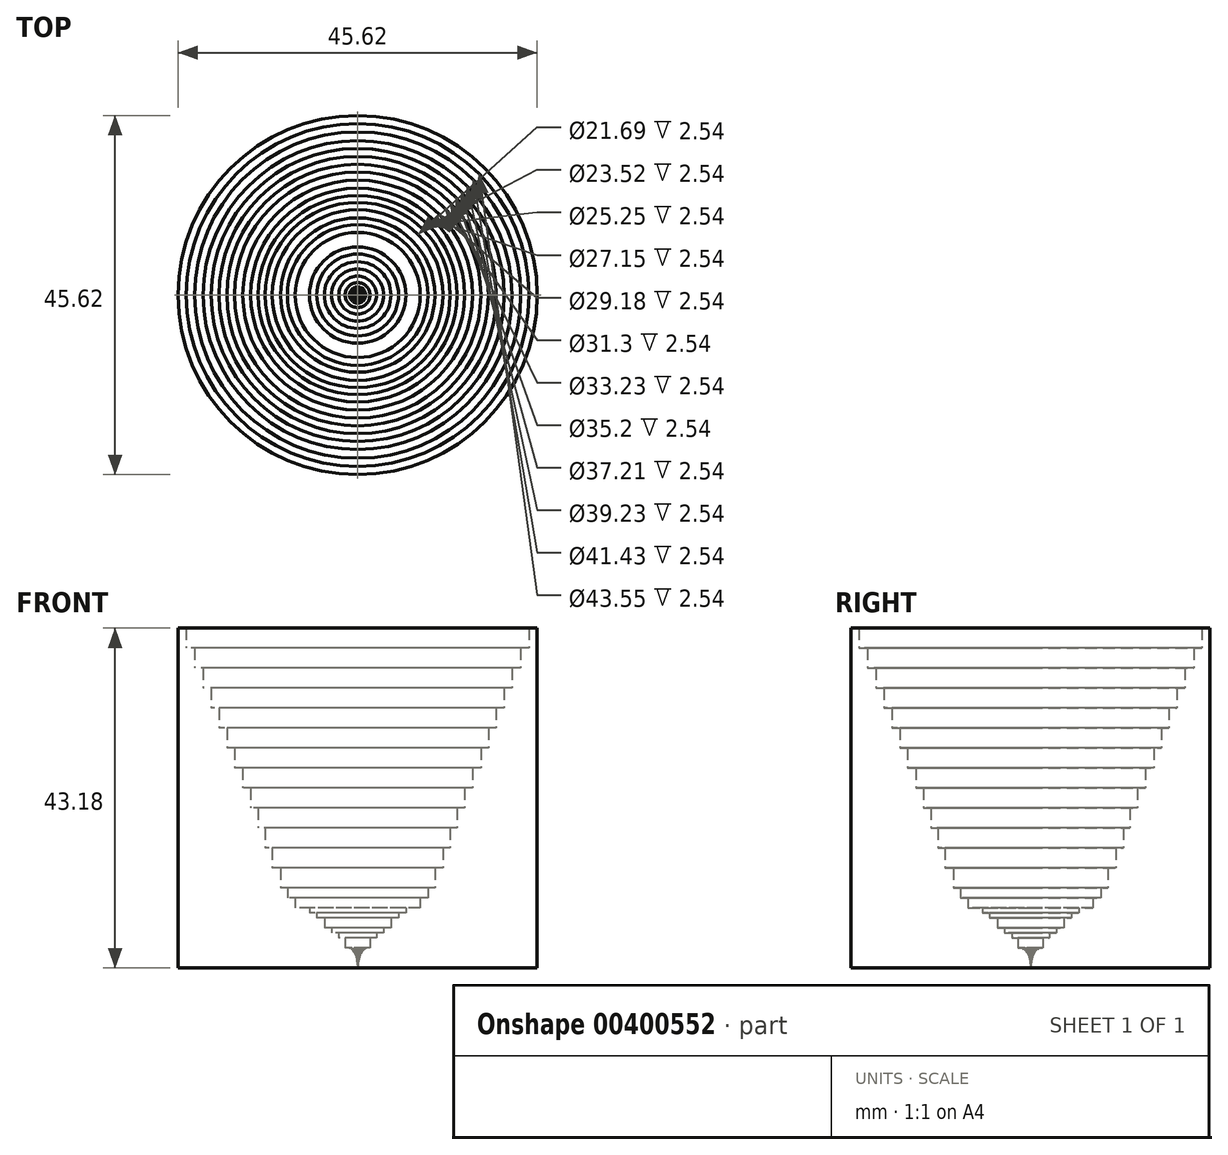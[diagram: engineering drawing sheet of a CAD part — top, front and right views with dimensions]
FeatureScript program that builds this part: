
annotation { "Feature Type Name" : "Feature", "Feature Type Description" : "" }
export const myFeature = defineFeature(function(context is Context, id is Id, definition is map)
    precondition{}
    {
        {
            var Q0;
            Q0=qCreatedBy(makeId("Top.planeOp"),FACE);
            var sketch = newSketch(context, id + "F0", { "sketchPlane" : qUnion([Q0])});
            skCircle(sketch, "E0", {"center": v(0, 0) * mm, "radius": 22.8 * mm});
            skCircle(sketch, "E1", {"center": v(0, 0) * mm, "radius": 21.78 * mm});
            skCircle(sketch, "E2", {"center": v(0, 0) * mm, "radius": 20.72 * mm});
            skCircle(sketch, "E3", {"center": v(0, 0) * mm, "radius": 19.62 * mm});
            skCircle(sketch, "E4", {"center": v(0, 0) * mm, "radius": 18.6 * mm});
            skCircle(sketch, "E5", {"center": v(0, 0) * mm, "radius": 17.6 * mm});
            skCircle(sketch, "E6", {"center": v(0, 0) * mm, "radius": 16.61 * mm});
            skCircle(sketch, "E7", {"center": v(0, 0) * mm, "radius": 15.65 * mm});
            skCircle(sketch, "E8", {"center": v(0, 0) * mm, "radius": 14.59 * mm});
            skCircle(sketch, "E9", {"center": v(0, 0) * mm, "radius": 13.57 * mm});
            skCircle(sketch, "E10", {"center": v(0, 0) * mm, "radius": 12.63 * mm});
            skCircle(sketch, "E11", {"center": v(0, 0) * mm, "radius": 11.76 * mm});
            skCircle(sketch, "E12", {"center": v(0, 0) * mm, "radius": 10.84 * mm});
            skCircle(sketch, "E13", {"center": v(0, 0) * mm, "radius": 9.8 * mm});
            skCircle(sketch, "E14", {"center": v(0, 0) * mm, "radius": 8.92 * mm});
            skCircle(sketch, "E15", {"center": v(0, 0) * mm, "radius": 7.94 * mm});
            skCircle(sketch, "E16", {"center": v(0, 0) * mm, "radius": 7.05 * mm});
            skCircle(sketch, "E17", {"center": v(0, 0) * mm, "radius": 6.12 * mm});
            skCircle(sketch, "E18", {"center": v(0, 0) * mm, "radius": 5.2 * mm});
            skCircle(sketch, "E19", {"center": v(0, 0) * mm, "radius": 4.23 * mm});
            skCircle(sketch, "E20", {"center": v(0, 0) * mm, "radius": 3.3 * mm});
            skCircle(sketch, "E21", {"center": v(0, 0) * mm, "radius": 2.4 * mm});
            skCircle(sketch, "E22", {"center": v(0, 0) * mm, "radius": 1.58 * mm});
            skCircle(sketch, "E23", {"center": v(0, 0) * mm, "radius": 1.03 * mm});
            skCircle(sketch, "E24", {"center": v(0, 0) * mm, "radius": 0.8 * mm});
            skCircle(sketch, "E25", {"center": v(0, 0) * mm, "radius": 0.67 * mm});
            skCircle(sketch, "E26", {"center": v(0, 0) * mm, "radius": 0.58 * mm});
            skCircle(sketch, "E27", {"center": v(0, 0) * mm, "radius": 0.49 * mm});
            skCircle(sketch, "E28", {"center": v(0, 0) * mm, "radius": 0.4 * mm});
            skCircle(sketch, "E29", {"center": v(0, 0) * mm, "radius": 0.34 * mm});
            skCircle(sketch, "E30", {"center": v(0, 0) * mm, "radius": 0.27 * mm});
            skCircle(sketch, "E31", {"center": v(0, 0) * mm, "radius": 0.22 * mm});
            skCircle(sketch, "E32", {"center": v(0, 0) * mm, "radius": 0.17 * mm});
            skCircle(sketch, "E33", {"center": v(0, 0) * mm, "radius": 0.11 * mm});
            skCircle(sketch, "E34", {"center": v(0, 0) * mm, "radius": 0.08 * mm});
            skCircle(sketch, "E35", {"center": v(0, 0) * mm, "radius": 0.06 * mm});
            skCircle(sketch, "E36", {"center": v(0, 0) * mm, "radius": 0.04 * mm});
            skCircle(sketch, "E37", {"center": v(0, 0) * mm, "radius": 0.03 * mm});
            skCircle(sketch, "E38", {"center": v(0, 0) * mm, "radius": 0.02 * mm});
            skSolve(sketch);
        }
        {
            var Q0;
            Q0=makeQuery(id+"F0.imprint","IMPRINT",FACE,{"disambiguationData":[TD([[makeQuery(id+"F0.imprint","IMPRINT",EDGE,{"derivedFrom":sQuery(id+"F0.wireOp",EDGE,"E38")}),1.0]])]});
            extrude(context, id + "F1", {"entities" : qUnion([Q0]), "depth" : 0.13 * mm});
        }
        {
            var Q0;
            Q0=makeQuery(id+"F0.imprint","IMPRINT",FACE,{"disambiguationData":[TD([[makeQuery(id+"F0.imprint","IMPRINT",EDGE,{"derivedFrom":sQuery(id+"F0.wireOp",EDGE,"E37")}),1.0]])]});
            extrude(context, id + "F2", {"entities" : qUnion([Q0]), "operationType" : NewBodyOperationType.ADD, "depth" : 0.25 * mm});
        }
        {
            var Q0;
            Q0=makeQuery(id+"F0.imprint","IMPRINT",FACE,{"disambiguationData":[TD([[makeQuery(id+"F0.imprint","IMPRINT",EDGE,{"derivedFrom":sQuery(id+"F0.wireOp",EDGE,"E36")}),1.0]])]});
            extrude(context, id + "F3", {"entities" : qUnion([Q0]), "operationType" : NewBodyOperationType.ADD, "depth" : 0.38 * mm});
        }
        {
            var Q0;
            Q0=makeQuery(id+"F0.imprint","IMPRINT",FACE,{"disambiguationData":[TD([[makeQuery(id+"F0.imprint","IMPRINT",EDGE,{"derivedFrom":sQuery(id+"F0.wireOp",EDGE,"E35")}),1.0]])]});
            extrude(context, id + "F4", {"entities" : qUnion([Q0]), "operationType" : NewBodyOperationType.ADD, "depth" : 0.5 * mm});
        }
        {
            var Q0;
            Q0=makeQuery(id+"F0.imprint","IMPRINT",FACE,{"disambiguationData":[TD([[makeQuery(id+"F0.imprint","IMPRINT",EDGE,{"derivedFrom":sQuery(id+"F0.wireOp",EDGE,"E34")}),1.0]])]});
            extrude(context, id + "F5", {"entities" : qUnion([Q0]), "operationType" : NewBodyOperationType.ADD, "depth" : 0.64 * mm});
        }
        {
            var Q0;
            Q0=makeQuery(id+"F0.imprint","IMPRINT",FACE,{"disambiguationData":[TD([[makeQuery(id+"F0.imprint","IMPRINT",EDGE,{"derivedFrom":sQuery(id+"F0.wireOp",EDGE,"E33")}),1.0]])]});
            extrude(context, id + "F6", {"entities" : qUnion([Q0]), "operationType" : NewBodyOperationType.ADD, "depth" : 0.76 * mm});
        }
        {
            var Q0;
            Q0=makeQuery(id+"F0.imprint","IMPRINT",FACE,{"disambiguationData":[TD([[makeQuery(id+"F0.imprint","IMPRINT",EDGE,{"derivedFrom":sQuery(id+"F0.wireOp",EDGE,"E32")}),1.0]])]});
            extrude(context, id + "F7", {"entities" : qUnion([Q0]), "operationType" : NewBodyOperationType.ADD, "depth" : 1.02 * mm});
        }
        {
            var Q0;
            Q0=makeQuery(id+"F0.imprint","IMPRINT",FACE,{"disambiguationData":[TD([[makeQuery(id+"F0.imprint","IMPRINT",EDGE,{"derivedFrom":sQuery(id+"F0.wireOp",EDGE,"E31")}),1.0]])]});
            extrude(context, id + "F8", {"entities" : qUnion([Q0]), "operationType" : NewBodyOperationType.ADD, "depth" : 1.27 * mm});
        }
        {
            var Q0;
            Q0=makeQuery(id+"F0.imprint","IMPRINT",FACE,{"disambiguationData":[TD([[makeQuery(id+"F0.imprint","IMPRINT",EDGE,{"derivedFrom":sQuery(id+"F0.wireOp",EDGE,"E30")}),1.0]])]});
            extrude(context, id + "F9", {"entities" : qUnion([Q0]), "operationType" : NewBodyOperationType.ADD, "depth" : 1.52 * mm});
        }
        {
            var Q0;
            Q0=makeQuery(id+"F0.imprint","IMPRINT",FACE,{"disambiguationData":[TD([[makeQuery(id+"F0.imprint","IMPRINT",EDGE,{"derivedFrom":sQuery(id+"F0.wireOp",EDGE,"E29")}),1.0]])]});
            extrude(context, id + "F10", {"entities" : qUnion([Q0]), "operationType" : NewBodyOperationType.ADD, "depth" : 1.65 * mm});
        }
        {
            var Q0;
            Q0=makeQuery(id+"F0.imprint","IMPRINT",FACE,{"disambiguationData":[TD([[makeQuery(id+"F0.imprint","IMPRINT",EDGE,{"derivedFrom":sQuery(id+"F0.wireOp",EDGE,"E28")}),1.0]])]});
            extrude(context, id + "F11", {"entities" : qUnion([Q0]), "operationType" : NewBodyOperationType.ADD, "depth" : 1.78 * mm});
        }
        {
            var Q0;
            Q0=makeQuery(id+"F0.imprint","IMPRINT",FACE,{"disambiguationData":[TD([[makeQuery(id+"F0.imprint","IMPRINT",EDGE,{"derivedFrom":sQuery(id+"F0.wireOp",EDGE,"E27")}),1.0]])]});
            extrude(context, id + "F12", {"entities" : qUnion([Q0]), "operationType" : NewBodyOperationType.ADD, "depth" : 1.9 * mm});
        }
        {
            var Q0;
            Q0=makeQuery(id+"F0.imprint","IMPRINT",FACE,{"disambiguationData":[TD([[makeQuery(id+"F0.imprint","IMPRINT",EDGE,{"derivedFrom":sQuery(id+"F0.wireOp",EDGE,"E26")}),1.0]])]});
            extrude(context, id + "F13", {"entities" : qUnion([Q0]), "operationType" : NewBodyOperationType.ADD, "depth" : 2.03 * mm});
        }
        {
            var Q0;
            Q0=makeQuery(id+"F0.imprint","IMPRINT",FACE,{"disambiguationData":[TD([[makeQuery(id+"F0.imprint","IMPRINT",EDGE,{"derivedFrom":sQuery(id+"F0.wireOp",EDGE,"E25")}),1.0]])]});
            extrude(context, id + "F14", {"entities" : qUnion([Q0]), "operationType" : NewBodyOperationType.ADD, "depth" : 2.16 * mm});
        }
        {
            var Q0;
            Q0=makeQuery(id+"F0.imprint","IMPRINT",FACE,{"disambiguationData":[TD([[makeQuery(id+"F0.imprint","IMPRINT",EDGE,{"derivedFrom":sQuery(id+"F0.wireOp",EDGE,"E24")}),1.0]])]});
            extrude(context, id + "F15", {"entities" : qUnion([Q0]), "operationType" : NewBodyOperationType.ADD, "depth" : 2.3 * mm});
        }
        {
            var Q0;
            Q0=makeQuery(id+"F0.imprint","IMPRINT",FACE,{"disambiguationData":[TD([[makeQuery(id+"F0.imprint","IMPRINT",EDGE,{"derivedFrom":sQuery(id+"F0.wireOp",EDGE,"E23")}),1.0]])]});
            extrude(context, id + "F16", {"entities" : qUnion([Q0]), "operationType" : NewBodyOperationType.ADD, "depth" : 2.41 * mm});
        }
        {
            var Q0;
            Q0=makeQuery(id+"F0.imprint","IMPRINT",FACE,{"disambiguationData":[TD([[makeQuery(id+"F0.imprint","IMPRINT",EDGE,{"derivedFrom":sQuery(id+"F0.wireOp",EDGE,"E22")}),1.0]])]});
            extrude(context, id + "F17", {"entities" : qUnion([Q0]), "operationType" : NewBodyOperationType.ADD, "depth" : 2.54 * mm});
        }
        {
            var Q0;
            Q0=makeQuery(id+"F0.imprint","IMPRINT",FACE,{"disambiguationData":[TD([[makeQuery(id+"F0.imprint","IMPRINT",EDGE,{"derivedFrom":sQuery(id+"F0.wireOp",EDGE,"E21")}),1.0]])]});
            extrude(context, id + "F18", {"entities" : qUnion([Q0]), "operationType" : NewBodyOperationType.ADD, "depth" : 3.8 * mm});
        }
        {
            var Q0;
            Q0=makeQuery(id+"F0.imprint","IMPRINT",FACE,{"disambiguationData":[TD([[makeQuery(id+"F0.imprint","IMPRINT",EDGE,{"derivedFrom":sQuery(id+"F0.wireOp",EDGE,"E20")}),1.0]])]});
            extrude(context, id + "F19", {"entities" : qUnion([Q0]), "operationType" : NewBodyOperationType.ADD, "depth" : 4.44 * mm});
        }
        {
            var Q0;
            Q0=makeQuery(id+"F0.imprint","IMPRINT",FACE,{"disambiguationData":[TD([[makeQuery(id+"F0.imprint","IMPRINT",EDGE,{"derivedFrom":sQuery(id+"F0.wireOp",EDGE,"E19")}),1.0]])]});
            extrude(context, id + "F20", {"entities" : qUnion([Q0]), "operationType" : NewBodyOperationType.ADD, "depth" : 5.08 * mm});
        }
        {
            var Q0;
            Q0=makeQuery(id+"F0.imprint","IMPRINT",FACE,{"disambiguationData":[TD([[makeQuery(id+"F0.imprint","IMPRINT",EDGE,{"derivedFrom":sQuery(id+"F0.wireOp",EDGE,"E18")}),1.0]])]});
            extrude(context, id + "F21", {"entities" : qUnion([Q0]), "operationType" : NewBodyOperationType.ADD, "depth" : 6.35 * mm});
        }
        {
            var Q0;
            Q0=makeQuery(id+"F0.imprint","IMPRINT",FACE,{"disambiguationData":[TD([[makeQuery(id+"F0.imprint","IMPRINT",EDGE,{"derivedFrom":sQuery(id+"F0.wireOp",EDGE,"E17")}),1.0]])]});
            extrude(context, id + "F22", {"entities" : qUnion([Q0]), "operationType" : NewBodyOperationType.ADD, "depth" : 7 * mm});
        }
        {
            var Q0;
            Q0=makeQuery(id+"F0.imprint","IMPRINT",FACE,{"disambiguationData":[TD([[makeQuery(id+"F0.imprint","IMPRINT",EDGE,{"derivedFrom":sQuery(id+"F0.wireOp",EDGE,"E16")}),1.0]])]});
            extrude(context, id + "F23", {"entities" : qUnion([Q0]), "operationType" : NewBodyOperationType.ADD, "depth" : 7.62 * mm});
        }
        {
            var Q0;
            Q0=makeQuery(id+"F0.imprint","IMPRINT",FACE,{"disambiguationData":[TD([[makeQuery(id+"F0.imprint","IMPRINT",EDGE,{"derivedFrom":sQuery(id+"F0.wireOp",EDGE,"E15")}),1.0]])]});
            extrude(context, id + "F24", {"entities" : qUnion([Q0]), "operationType" : NewBodyOperationType.ADD, "depth" : 7.62 * mm});
        }
        {
            var Q0;
            Q0=makeQuery(id+"F0.imprint","IMPRINT",FACE,{"disambiguationData":[TD([[makeQuery(id+"F0.imprint","IMPRINT",EDGE,{"derivedFrom":sQuery(id+"F0.wireOp",EDGE,"E14")}),1.0]])]});
            extrude(context, id + "F25", {"entities" : qUnion([Q0]), "operationType" : NewBodyOperationType.ADD, "depth" : 8.9 * mm});
        }
        {
            var Q0;
            Q0=makeQuery(id+"F0.imprint","IMPRINT",FACE,{"disambiguationData":[TD([[makeQuery(id+"F0.imprint","IMPRINT",EDGE,{"derivedFrom":sQuery(id+"F0.wireOp",EDGE,"E13")}),1.0]])]});
            extrude(context, id + "F26", {"entities" : qUnion([Q0]), "operationType" : NewBodyOperationType.ADD, "depth" : 10.16 * mm});
        }
        {
            var Q0;
            Q0=makeQuery(id+"F0.imprint","IMPRINT",FACE,{"disambiguationData":[TD([[makeQuery(id+"F0.imprint","IMPRINT",EDGE,{"derivedFrom":sQuery(id+"F0.wireOp",EDGE,"E12")}),1.0]])]});
            extrude(context, id + "F27", {"entities" : qUnion([Q0]), "operationType" : NewBodyOperationType.ADD, "depth" : 12.7 * mm});
        }
        {
            var Q0;
            Q0=makeQuery(id+"F0.imprint","IMPRINT",FACE,{"disambiguationData":[TD([[makeQuery(id+"F0.imprint","IMPRINT",EDGE,{"derivedFrom":sQuery(id+"F0.wireOp",EDGE,"E11")}),1.0]])]});
            extrude(context, id + "F28", {"entities" : qUnion([Q0]), "operationType" : NewBodyOperationType.ADD, "depth" : 15.24 * mm});
        }
        {
            var Q0;
            Q0=makeQuery(id+"F0.imprint","IMPRINT",FACE,{"disambiguationData":[TD([[makeQuery(id+"F0.imprint","IMPRINT",EDGE,{"derivedFrom":sQuery(id+"F0.wireOp",EDGE,"E10")}),1.0]])]});
            extrude(context, id + "F29", {"entities" : qUnion([Q0]), "operationType" : NewBodyOperationType.ADD, "depth" : 17.78 * mm});
        }
        {
            var Q0;
            Q0=makeQuery(id+"F0.imprint","IMPRINT",FACE,{"disambiguationData":[TD([[makeQuery(id+"F0.imprint","IMPRINT",EDGE,{"derivedFrom":sQuery(id+"F0.wireOp",EDGE,"E9")}),1.0]])]});
            extrude(context, id + "F30", {"entities" : qUnion([Q0]), "operationType" : NewBodyOperationType.ADD, "depth" : 20.32 * mm});
        }
        {
            var Q0;
            Q0=makeQuery(id+"F0.imprint","IMPRINT",FACE,{"disambiguationData":[TD([[makeQuery(id+"F0.imprint","IMPRINT",EDGE,{"derivedFrom":sQuery(id+"F0.wireOp",EDGE,"E8")}),1.0]])]});
            extrude(context, id + "F31", {"entities" : qUnion([Q0]), "operationType" : NewBodyOperationType.ADD, "depth" : 22.86 * mm});
        }
        {
            var Q0;
            Q0=makeQuery(id+"F0.imprint","IMPRINT",FACE,{"disambiguationData":[TD([[makeQuery(id+"F0.imprint","IMPRINT",EDGE,{"derivedFrom":sQuery(id+"F0.wireOp",EDGE,"E7")}),1.0]])]});
            extrude(context, id + "F32", {"entities" : qUnion([Q0]), "operationType" : NewBodyOperationType.ADD, "depth" : 25.4 * mm});
        }
        {
            var Q0;
            Q0=makeQuery(id+"F0.imprint","IMPRINT",FACE,{"disambiguationData":[TD([[makeQuery(id+"F0.imprint","IMPRINT",EDGE,{"derivedFrom":sQuery(id+"F0.wireOp",EDGE,"E6")}),1.0]])]});
            extrude(context, id + "F33", {"entities" : qUnion([Q0]), "operationType" : NewBodyOperationType.ADD, "depth" : 27.94 * mm});
        }
        {
            var Q0;
            Q0=makeQuery(id+"F0.imprint","IMPRINT",FACE,{"disambiguationData":[TD([[makeQuery(id+"F0.imprint","IMPRINT",EDGE,{"derivedFrom":sQuery(id+"F0.wireOp",EDGE,"E5")}),1.0]])]});
            extrude(context, id + "F34", {"entities" : qUnion([Q0]), "operationType" : NewBodyOperationType.ADD, "depth" : 30.48 * mm});
        }
        {
            var Q0;
            Q0=makeQuery(id+"F0.imprint","IMPRINT",FACE,{"disambiguationData":[TD([[makeQuery(id+"F0.imprint","IMPRINT",EDGE,{"derivedFrom":sQuery(id+"F0.wireOp",EDGE,"E4")}),1.0]])]});
            extrude(context, id + "F35", {"entities" : qUnion([Q0]), "operationType" : NewBodyOperationType.ADD, "depth" : 33.02 * mm});
        }
        {
            var Q0;
            Q0=makeQuery(id+"F0.imprint","IMPRINT",FACE,{"disambiguationData":[TD([[makeQuery(id+"F0.imprint","IMPRINT",EDGE,{"derivedFrom":sQuery(id+"F0.wireOp",EDGE,"E3")}),1.0]])]});
            extrude(context, id + "F36", {"entities" : qUnion([Q0]), "operationType" : NewBodyOperationType.ADD, "depth" : 35.56 * mm});
        }
        {
            var Q0;
            Q0=makeQuery(id+"F0.imprint","IMPRINT",FACE,{"disambiguationData":[TD([[makeQuery(id+"F0.imprint","IMPRINT",EDGE,{"derivedFrom":sQuery(id+"F0.wireOp",EDGE,"E2")}),1.0]])]});
            extrude(context, id + "F37", {"entities" : qUnion([Q0]), "operationType" : NewBodyOperationType.ADD, "depth" : 38.1 * mm});
        }
        {
            var Q0;
            Q0=makeQuery(id+"F0.imprint","IMPRINT",FACE,{"disambiguationData":[TD([[makeQuery(id+"F0.imprint","IMPRINT",EDGE,{"derivedFrom":sQuery(id+"F0.wireOp",EDGE,"E1")}),1.0]])]});
            extrude(context, id + "F38", {"entities" : qUnion([Q0]), "operationType" : NewBodyOperationType.ADD, "depth" : 40.64 * mm});
        }
        {
            var Q0;
            Q0=makeQuery(id+"F0.imprint","IMPRINT",FACE,{"disambiguationData":[TD([[makeQuery(id+"F0.imprint","IMPRINT",EDGE,{"derivedFrom":sQuery(id+"F0.wireOp",EDGE,"E0")}),1.0]])]});
            extrude(context, id + "F39", {"entities" : qUnion([Q0]), "operationType" : NewBodyOperationType.ADD, "depth" : 43.18 * mm});
        }
    });
